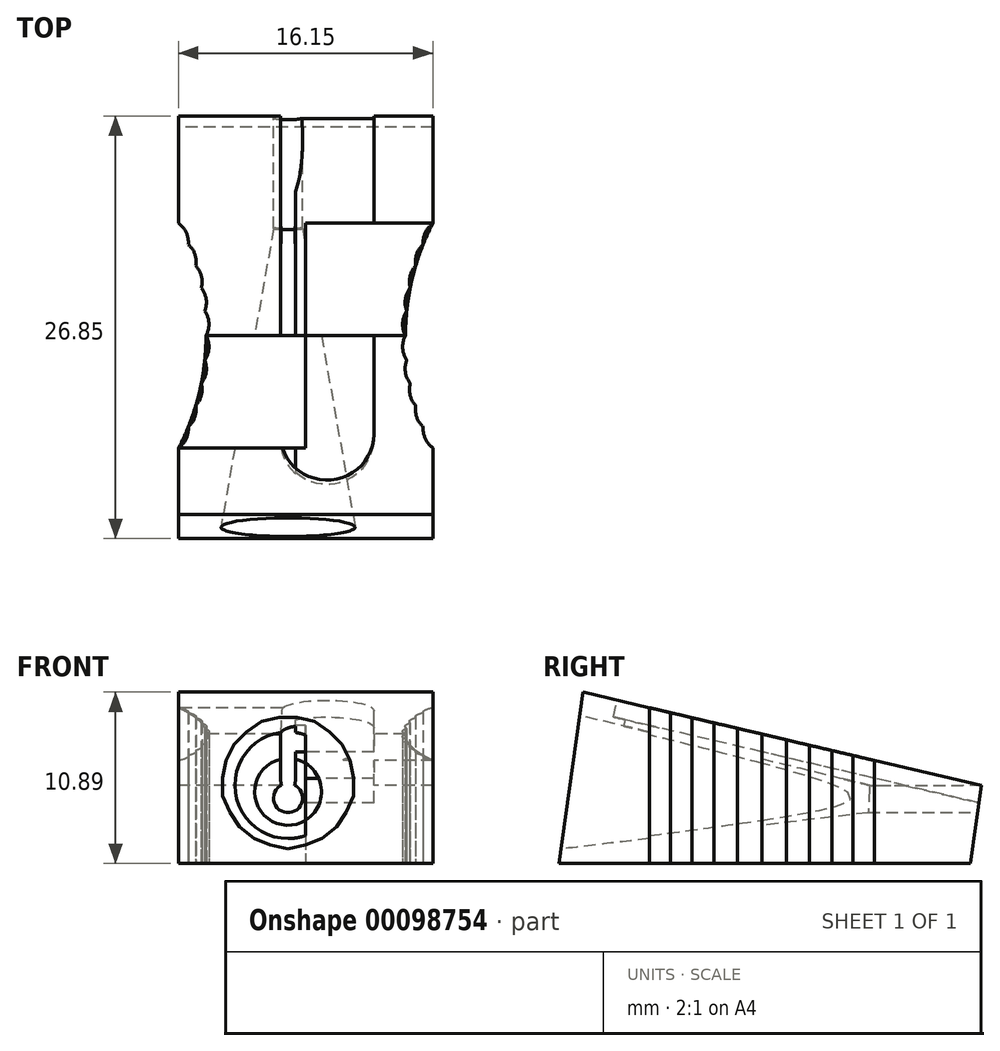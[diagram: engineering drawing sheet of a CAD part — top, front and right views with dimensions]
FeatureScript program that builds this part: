
annotation { "Feature Type Name" : "Feature", "Feature Type Description" : "" }
export const myFeature = defineFeature(function(context is Context, id is Id, definition is map)
    precondition{}
    {
        {
            var Q0;
            Q0=qCreatedBy(makeId("Right.planeOp"),FACE);
            var sketch = newSketch(context, id + "F0", { "sketchPlane" : qUnion([Q0])});
            skLineSegment(sketch, "E0.bottom", {"start": v(0, 0) * mm, "end": v(26.15, 0) * mm});
            skLineSegment(sketch, "E0.top", {"start": v(1.53, 10.9) * mm, "end": v(27.68, 10.9) * mm});
            skLineSegment(sketch, "E0.left", {"start": v(0, 0) * mm, "end": v(1.53, 10.9) * mm});
            skLineSegment(sketch, "E0.right", {"start": v(26.15, 0) * mm, "end": v(27.68, 10.9) * mm});
            skLineSegment(sketch, "E1", {"start": v(26.15, 0) * mm, "end": v(26.85, 4.95) * mm});
            skLineSegment(sketch, "E2", {"start": v(1.53, 10.9) * mm, "end": v(26.85, 4.95) * mm});
            skSolve(sketch);
        }
        {
            var Q0;
            Q0 = qSketchRegion(id + "F0", true);
            extrude(context, id + "F1", {"entities" : qUnion([Q0]), "depth" : 16.15 * mm});
        }
        {
            var Q0;
            Q0=makeQuery(id+"F0.imprint","IMPRINT",FACE,{"disambiguationData":[TD([[makeQuery(id+"F0.imprint","IMPRINT",EDGE,{"derivedFrom":sQuery(id+"F0.wireOp",EDGE,"E0.top")}),-1.0]])]});
            extrude(context, id + "F2", {"entities" : qUnion([Q0]), "operationType" : NewBodyOperationType.REMOVE, "depth" : 16.15 * mm});
        }
        {
            var Q0;
            Q0=qCreatedBy(makeId("Right.planeOp"),FACE);
            cPlane(context, id + "F3", {"entities" : qUnion([Q0]), "cplaneType" : CPlaneType.OFFSET, "offset" : 6.95 * mm, "width" : 150 * mm, "height" : 150 * mm});
        }
        {
            var Q0;
            Q0=qCreatedBy(id+"F3.planeOp",FACE);
            var sketch = newSketch(context, id + "F4", { "sketchPlane" : qUnion([Q0])});
            skLineSegment(sketch, "E3", {"start": v(0, 9.71) * mm, "end": v(19.75, 5.08) * mm});
            skLineSegment(sketch, "E4", {"start": v(19.75, 5.08) * mm, "end": v(19.75, 4.15) * mm});
            skLineSegment(sketch, "E5", {"start": v(19.75, 4.15) * mm, "end": v(0.73, 5.23) * mm});
            skLineSegment(sketch, "E6", {"start": v(0, 9.71) * mm, "end": v(0.73, 5.23) * mm});
            skLineSegment(sketch, "E7", {"start": v(19.75, 4.15) * mm, "end": v(19.75, 5.08) * mm});
            skSolve(sketch);
        }
        {
            var Q0;
            Q0=makeQuery(id+"F4.imprint","IMPRINT",FACE,{"disambiguationData":[TD([[makeQuery(id+"F4.imprint","IMPRINT",EDGE,{"derivedFrom":sQuery(id+"F4.wireOp",EDGE,"E3")}),-1.0]])]});
            var Q1;
            Q1=sQuery(id+"F4.wireOp",EDGE,"E5");
            revolve(context, id + "F5", {"operationType" : NewBodyOperationType.REMOVE, "entities" : qUnion([Q0]), "axis" : qUnion([Q1]), "revolveType" : RevolveType.FULL, "oppositeDirection" : true});
        }
        {
            var Q0;
            Q0=qCreatedBy(id+"F3.planeOp",FACE);
            var sketch = newSketch(context, id + "F6", { "sketchPlane" : qUnion([Q0])});
            skLineSegment(sketch, "E8", {"start": v(19.63, 4.17) * mm, "end": v(19.63, 5.08) * mm});
            skLineSegment(sketch, "E9", {"start": v(19.63, 5.08) * mm, "end": v(27.4, 5.1) * mm});
            skLineSegment(sketch, "E10", {"start": v(27.4, 5.1) * mm, "end": v(27.4, 4.17) * mm});
            skLineSegment(sketch, "E11", {"start": v(27.4, 4.17) * mm, "end": v(19.63, 4.17) * mm});
            skSolve(sketch);
        }
        {
            var Q0;
            Q0=makeQuery(id+"F6.imprint","IMPRINT",FACE,{"disambiguationData":[TD([[makeQuery(id+"F6.imprint","IMPRINT",EDGE,{"derivedFrom":sQuery(id+"F6.wireOp",EDGE,"E8")}),-1.0]])]});
            var Q1;
            Q1=sQuery(id+"F6.wireOp",EDGE,"E11");
            revolve(context, id + "F7", {"operationType" : NewBodyOperationType.REMOVE, "entities" : qUnion([Q0]), "axis" : qUnion([Q1]), "revolveType" : RevolveType.FULL, "oppositeDirection" : true});
        }
        {
            var Q0;
            Q0=makeQuery(id+"F2.boolean.opBoolean","COPY",FACE,{"derivedFrom":makeQuery(id+"F2.opExtrude","SWEPT_FACE",FACE,{"disambiguationData":[OSD([sQuery(id+"F0.wireOp",EDGE,"E2")])]})});
            var sketch = newSketch(context, id + "F8", { "sketchPlane" : qUnion([Q0])});
            skLineSegment(sketch, "E12", {"start": v(6.46, 25) * mm, "end": v(6.46, 4.22) * mm});
            skLineSegment(sketch, "E13", {"start": v(12.4, 25) * mm, "end": v(12.4, 4.22) * mm});
            skArc(sketch, "E14", {"start": v(6.46, 4.22) * mm, "mid": v(9.43, 1.25) * mm, "end": v(12.4, 4.22) * mm});
            skSolve(sketch);
        }
        {
            var Q0;
            Q0=makeQuery(id+"F8.imprint","IMPRINT",FACE,{"disambiguationData":[TD([[makeQuery(id+"F8.imprint","IMPRINT",EDGE,{"derivedFrom":sQuery(id+"F8.wireOp",EDGE,"E12")}),1.0]])]});
            extrude(context, id + "F9", {"entities" : qUnion([Q0]), "operationType" : NewBodyOperationType.REMOVE, "oppositeDirection" : true, "depth" : 1.1 * mm});
        }
        {
            var Q0;
            Q0=makeQuery(id+"F8.imprint","IMPRINT",FACE,{"disambiguationData":[TD([[makeQuery(id+"F8.imprint","IMPRINT",EDGE,{"derivedFrom":sQuery(id+"F8.wireOp",EDGE,"E12")}),1.0]])]});
            var sketch = newSketch(context, id + "F10", { "sketchPlane" : qUnion([Q0])});
            skLineSegment(sketch, "E15", {"start": v(7.44, 25) * mm, "end": v(7.44, 2.02) * mm});
            skSolve(sketch);
        }
        {
            var Q0;
            {var subQ0=sQuery(id+"F10.wireOp",EDGE,"E15");Q0=makeQuery(id+"F10.imprint","IMPRINT",FACE,{"disambiguationData":[TD([[makeQuery(id+"F10.imprint","IMPRINT",EDGE,{"derivedFrom":subQ0}),-1.0]])]});}
            extrude(context, id + "F11", {"entities" : qUnion([Q0]), "operationType" : NewBodyOperationType.REMOVE, "oppositeDirection" : true, "depth" : 1.6 * mm});
        }
        {
            var Q0;
            Q0=makeQuery(id+"F1.opExtrude","SWEPT_FACE",FACE,{"disambiguationData":[OSD([sQuery(id+"F0.wireOp",EDGE,"E0.bottom")])]});
            var sketch = newSketch(context, id + "F12", { "sketchPlane" : qUnion([Q0])});
            skArc(sketch, "E16", {"start": v(0, -20.03) * mm, "mid": v(1.74, -12.9) * mm, "end": v(0, -5.76) * mm});
            skArc(sketch, "E17", {"start": v(16.15, -5.76) * mm, "mid": v(14.41, -12.9) * mm, "end": v(16.15, -20.03) * mm});
            skSolve(sketch);
        }
        {
            var Q0;
            {var subQ0=sQuery(id+"F12.wireOp",EDGE,"E16");Q0=makeQuery(id+"F12.imprint","IMPRINT",FACE,{"disambiguationData":[TD([[makeQuery(id+"F12.imprint","IMPRINT",EDGE,{"derivedFrom":subQ0}),1.0]])]});}
            var Q1;
            {var subQ0=sQuery(id+"F12.wireOp",EDGE,"E17");Q1=makeQuery(id+"F12.imprint","IMPRINT",FACE,{"disambiguationData":[TD([[makeQuery(id+"F12.imprint","IMPRINT",EDGE,{"derivedFrom":subQ0}),1.0]])]});}
            extrude(context, id + "F13", {"entities" : qUnion([Q0, Q1]), "operationType" : NewBodyOperationType.REMOVE, "oppositeDirection" : true, "depth" : 10 * mm});
        }
        {
            var Q0;
            Q0=makeQuery(id+"F9.boolean.opBoolean","COPY",FACE,{"derivedFrom":makeQuery(id+"F9.opExtrude","CAP_FACE",FACE,{"disambiguationData":[OSD([sQuery(id+"F0.wireOp",EDGE,"E0.right"),sQuery(id+"F0.wireOp",EDGE,"E1"),sQuery(id+"F0.wireOp",EDGE,"E2"),sQuery(id+"F6.wireOp",EDGE,"E9"),sQuery(id+"F8.wireOp",EDGE,"E12"),sQuery(id+"F8.wireOp",EDGE,"E13"),sQuery(id+"F8.wireOp",EDGE,"E14")])],"isStart":false})});
            var sketch = newSketch(context, id + "F14", { "sketchPlane" : qUnion([Q0])});
            skLineSegment(sketch, "E18", {"start": v(12.4, 25) * mm, "end": v(12.4, 4.22) * mm});
            skLineSegment(sketch, "E19", {"start": v(7.44, 25) * mm, "end": v(7.83, 25) * mm});
            skLineSegment(sketch, "E20", {"start": v(7.83, 25) * mm, "end": v(7.83, 1.72) * mm});
            skSolve(sketch);
        }
        {
            var Q0;
            Q0=makeQuery(id+"F9.boolean.opBoolean","COPY",FACE,{"derivedFrom":makeQuery(id+"F9.opExtrude","SWEPT_FACE",FACE,{"disambiguationData":[OSD([sQuery(id+"F0.wireOp",EDGE,"E0.right"),sQuery(id+"F0.wireOp",EDGE,"E1"),sQuery(id+"F0.wireOp",EDGE,"E2")])]})});
            extrude(context, id + "F15", {"entities" : qUnion([Q0]), "operationType" : NewBodyOperationType.REMOVE, "oppositeDirection" : true, "depth" : 25 * mm});
        }
        {
            var Q0;
            {var subQ0=sQuery(id+"F14.wireOp",EDGE,"E18");Q0=makeQuery(id+"F14.imprint","IMPRINT",FACE,{"disambiguationData":[TD([[makeQuery(id+"F14.imprint","IMPRINT",EDGE,{"derivedFrom":subQ0}),-1.0]])]});}
            var sketch = newSketch(context, id + "F16", { "sketchPlane" : qUnion([Q0])});
            skCircle(sketch, "E21", {"center": v(10.67, 12.1) * mm, "radius": 1.08 * mm});
            skSolve(sketch);
        }
        {
            var Q0;
            Q0=makeQuery(id+"F16.imprint","IMPRINT",FACE,{"disambiguationData":[TD([[makeQuery(id+"F16.imprint","IMPRINT",EDGE,{"derivedFrom":sQuery(id+"F16.wireOp",EDGE,"E21")}),1.0]])]});
            extrude(context, id + "F17", {"entities" : qUnion([Q0]), "operationType" : NewBodyOperationType.REMOVE, "oppositeDirection" : true, "depth" : .5 * mm});
        }
        {
            var Q0;
            Q0=makeQuery(id+"F1.opExtrude","SWEPT_FACE",FACE,{"disambiguationData":[OSD([sQuery(id+"F0.wireOp",EDGE,"E0.bottom")])]});
            var sketch = newSketch(context, id + "F18", { "sketchPlane" : qUnion([Q0])});
            skLineSegment(sketch, "E22", {"start": v(1.74, -12.9) * mm, "end": v(14.41, -12.9) * mm});
            skLineSegment(sketch, "E23", {"start": v(0, -5.76) * mm, "end": v(16.15, -5.76) * mm});
            skLineSegment(sketch, "E24", {"start": v(0, -20.03) * mm, "end": v(16.15, -20.03) * mm});
            skLineSegment(sketch, "E25", {"start": v(8.07, -5.76) * mm, "end": v(8.07, -20.03) * mm});
            skLineSegment(sketch, "E26.MirrorCS", {"start": v(14.41, -12.9) * mm, "end": v(1.74, -12.9) * mm});
            skPoint(sketch, "E27", {"position": v(0.61, -18.7) * mm});
            skPoint(sketch, "E28", {"position": v(1.1, -17.33) * mm});
            skPoint(sketch, "E29", {"position": v(1.44, -15.93) * mm});
            skPoint(sketch, "E30", {"position": v(1.66, -14.46) * mm});
            skArc(sketch, "E31", {"start": v(0, -20.03) * mm, "mid": v(0.49, -19.44) * mm, "end": v(0.61, -18.7) * mm});
            skArc(sketch, "E32", {"start": v(0.61, -18.7) * mm, "mid": v(1.03, -18.07) * mm, "end": v(1.1, -17.33) * mm});
            skArc(sketch, "E33", {"start": v(1.1, -17.33) * mm, "mid": v(1.45, -16.68) * mm, "end": v(1.44, -15.93) * mm});
            skArc(sketch, "E34", {"start": v(1.44, -15.93) * mm, "mid": v(1.75, -15.22) * mm, "end": v(1.66, -14.46) * mm});
            skArc(sketch, "E35", {"start": v(1.66, -14.46) * mm, "mid": v(1.92, -13.69) * mm, "end": v(1.74, -12.9) * mm});
            skArc(sketch, "E36", {"start": v(-0.86, -18.83) * mm, "mid": v(0.02, -16.28) * mm, "end": v(0.45, -13.61) * mm, "construction": true});
            skArc(sketch, "E37.MirrorCS", {"start": v(1.66, -11.34) * mm, "mid": v(1.92, -12.1) * mm, "end": v(1.74, -12.9) * mm});
            skArc(sketch, "E38.MirrorCS", {"start": v(1.44, -9.87) * mm, "mid": v(1.75, -10.57) * mm, "end": v(1.66, -11.34) * mm});
            skArc(sketch, "E39.MirrorCS", {"start": v(1.1, -8.46) * mm, "mid": v(1.45, -9.12) * mm, "end": v(1.44, -9.87) * mm});
            skArc(sketch, "E40.MirrorCS", {"start": v(0.61, -7.1) * mm, "mid": v(1.03, -7.72) * mm, "end": v(1.1, -8.46) * mm});
            skArc(sketch, "E41.MirrorCS", {"start": v(0, -5.76) * mm, "mid": v(0.49, -6.35) * mm, "end": v(0.61, -7.1) * mm});
            skArc(sketch, "E42.MirrorCS", {"start": v(16.15, -5.76) * mm, "mid": v(15.66, -6.35) * mm, "end": v(15.54, -7.1) * mm});
            skArc(sketch, "E43.MirrorCS", {"start": v(15.54, -7.1) * mm, "mid": v(15.12, -7.72) * mm, "end": v(15.06, -8.46) * mm});
            skArc(sketch, "E44.MirrorCS", {"start": v(15.06, -8.46) * mm, "mid": v(14.7, -9.12) * mm, "end": v(14.71, -9.87) * mm});
            skArc(sketch, "E45.MirrorCS", {"start": v(14.71, -9.87) * mm, "mid": v(14.4, -10.57) * mm, "end": v(14.5, -11.34) * mm});
            skArc(sketch, "E46.MirrorCS", {"start": v(14.5, -11.34) * mm, "mid": v(14.23, -12.1) * mm, "end": v(14.41, -12.9) * mm});
            skArc(sketch, "E47.MirrorCS", {"start": v(14.5, -14.46) * mm, "mid": v(14.23, -13.69) * mm, "end": v(14.41, -12.9) * mm});
            skArc(sketch, "E48.MirrorCS", {"start": v(14.71, -15.93) * mm, "mid": v(14.4, -15.22) * mm, "end": v(14.5, -14.46) * mm});
            skArc(sketch, "E49.MirrorCS", {"start": v(15.06, -17.33) * mm, "mid": v(14.7, -16.68) * mm, "end": v(14.71, -15.93) * mm});
            skArc(sketch, "E50.MirrorCS", {"start": v(15.54, -18.7) * mm, "mid": v(15.12, -18.07) * mm, "end": v(15.06, -17.33) * mm});
            skArc(sketch, "E51.MirrorCS", {"start": v(16.15, -20.03) * mm, "mid": v(15.66, -19.44) * mm, "end": v(15.54, -18.7) * mm});
            skSolve(sketch);
        }
        {
            var Q0;
            {var subQ0=sQuery(id+"F18.wireOp",EDGE,"E35");Q0=makeQuery(id+"F18.imprint","IMPRINT",FACE,{"disambiguationData":[TD([[makeQuery(id+"F18.imprint","IMPRINT",EDGE,{"derivedFrom":subQ0}),1.0]])]});}
            var Q1;
            {var subQ0=sQuery(id+"F18.wireOp",EDGE,"E34");Q1=makeQuery(id+"F18.imprint","IMPRINT",FACE,{"disambiguationData":[TD([[makeQuery(id+"F18.imprint","IMPRINT",EDGE,{"derivedFrom":subQ0}),1.0]])]});}
            var Q2;
            {var subQ0=sQuery(id+"F18.wireOp",EDGE,"E33");Q2=makeQuery(id+"F18.imprint","IMPRINT",FACE,{"disambiguationData":[TD([[makeQuery(id+"F18.imprint","IMPRINT",EDGE,{"derivedFrom":subQ0}),1.0]])]});}
            var Q3;
            {var subQ0=sQuery(id+"F18.wireOp",EDGE,"E32");Q3=makeQuery(id+"F18.imprint","IMPRINT",FACE,{"disambiguationData":[TD([[makeQuery(id+"F18.imprint","IMPRINT",EDGE,{"derivedFrom":subQ0}),1.0]])]});}
            var Q4;
            {var subQ0=sQuery(id+"F18.wireOp",EDGE,"E31");Q4=makeQuery(id+"F18.imprint","IMPRINT",FACE,{"disambiguationData":[TD([[makeQuery(id+"F18.imprint","IMPRINT",EDGE,{"derivedFrom":subQ0}),1.0]])]});}
            var Q5;
            {var subQ0=sQuery(id+"F18.wireOp",EDGE,"E37.MirrorCS");Q5=makeQuery(id+"F18.imprint","IMPRINT",FACE,{"disambiguationData":[TD([[makeQuery(id+"F18.imprint","IMPRINT",EDGE,{"derivedFrom":subQ0}),-1.0]])]});}
            var Q6;
            {var subQ0=sQuery(id+"F18.wireOp",EDGE,"E38.MirrorCS");Q6=makeQuery(id+"F18.imprint","IMPRINT",FACE,{"disambiguationData":[TD([[makeQuery(id+"F18.imprint","IMPRINT",EDGE,{"derivedFrom":subQ0}),-1.0]])]});}
            var Q7;
            {var subQ0=sQuery(id+"F18.wireOp",EDGE,"E39.MirrorCS");Q7=makeQuery(id+"F18.imprint","IMPRINT",FACE,{"disambiguationData":[TD([[makeQuery(id+"F18.imprint","IMPRINT",EDGE,{"derivedFrom":subQ0}),-1.0]])]});}
            var Q8;
            {var subQ0=sQuery(id+"F18.wireOp",EDGE,"E40.MirrorCS");Q8=makeQuery(id+"F18.imprint","IMPRINT",FACE,{"disambiguationData":[TD([[makeQuery(id+"F18.imprint","IMPRINT",EDGE,{"derivedFrom":subQ0}),-1.0]])]});}
            var Q9;
            {var subQ0=sQuery(id+"F18.wireOp",EDGE,"E41.MirrorCS");Q9=makeQuery(id+"F18.imprint","IMPRINT",FACE,{"disambiguationData":[TD([[makeQuery(id+"F18.imprint","IMPRINT",EDGE,{"derivedFrom":subQ0}),-1.0]])]});}
            var Q10;
            {var subQ0=sQuery(id+"F18.wireOp",EDGE,"E42.MirrorCS");Q10=makeQuery(id+"F18.imprint","IMPRINT",FACE,{"disambiguationData":[TD([[makeQuery(id+"F18.imprint","IMPRINT",EDGE,{"derivedFrom":subQ0}),1.0]])]});}
            var Q11;
            {var subQ0=sQuery(id+"F18.wireOp",EDGE,"E43.MirrorCS");Q11=makeQuery(id+"F18.imprint","IMPRINT",FACE,{"disambiguationData":[TD([[makeQuery(id+"F18.imprint","IMPRINT",EDGE,{"derivedFrom":subQ0}),1.0]])]});}
            var Q12;
            {var subQ0=sQuery(id+"F18.wireOp",EDGE,"E44.MirrorCS");Q12=makeQuery(id+"F18.imprint","IMPRINT",FACE,{"disambiguationData":[TD([[makeQuery(id+"F18.imprint","IMPRINT",EDGE,{"derivedFrom":subQ0}),1.0]])]});}
            var Q13;
            {var subQ0=sQuery(id+"F18.wireOp",EDGE,"E45.MirrorCS");Q13=makeQuery(id+"F18.imprint","IMPRINT",FACE,{"disambiguationData":[TD([[makeQuery(id+"F18.imprint","IMPRINT",EDGE,{"derivedFrom":subQ0}),1.0]])]});}
            var Q14;
            {var subQ0=sQuery(id+"F18.wireOp",EDGE,"E46.MirrorCS");Q14=makeQuery(id+"F18.imprint","IMPRINT",FACE,{"disambiguationData":[TD([[makeQuery(id+"F18.imprint","IMPRINT",EDGE,{"derivedFrom":subQ0}),1.0]])]});}
            var Q15;
            {var subQ0=sQuery(id+"F18.wireOp",EDGE,"E47.MirrorCS");Q15=makeQuery(id+"F18.imprint","IMPRINT",FACE,{"disambiguationData":[TD([[makeQuery(id+"F18.imprint","IMPRINT",EDGE,{"derivedFrom":subQ0}),-1.0]])]});}
            var Q16;
            {var subQ0=sQuery(id+"F18.wireOp",EDGE,"E48.MirrorCS");Q16=makeQuery(id+"F18.imprint","IMPRINT",FACE,{"disambiguationData":[TD([[makeQuery(id+"F18.imprint","IMPRINT",EDGE,{"derivedFrom":subQ0}),-1.0]])]});}
            var Q17;
            {var subQ0=sQuery(id+"F18.wireOp",EDGE,"E49.MirrorCS");Q17=makeQuery(id+"F18.imprint","IMPRINT",FACE,{"disambiguationData":[TD([[makeQuery(id+"F18.imprint","IMPRINT",EDGE,{"derivedFrom":subQ0}),-1.0]])]});}
            var Q18;
            {var subQ0=sQuery(id+"F18.wireOp",EDGE,"E50.MirrorCS");Q18=makeQuery(id+"F18.imprint","IMPRINT",FACE,{"disambiguationData":[TD([[makeQuery(id+"F18.imprint","IMPRINT",EDGE,{"derivedFrom":subQ0}),-1.0]])]});}
            var Q19;
            {var subQ0=sQuery(id+"F18.wireOp",EDGE,"E51.MirrorCS");Q19=makeQuery(id+"F18.imprint","IMPRINT",FACE,{"disambiguationData":[TD([[makeQuery(id+"F18.imprint","IMPRINT",EDGE,{"derivedFrom":subQ0}),-1.0]])]});}
            extrude(context, id + "F19", {"entities" : qUnion([Q0, Q1, Q2, Q3, Q4, Q5, Q6, Q7, Q8, Q9, Q10, Q11, Q12, Q13, Q14, Q15, Q16, Q17, Q18, Q19]), "operationType" : NewBodyOperationType.REMOVE, "oppositeDirection" : true, "depth" : 10 * mm});
        }
    });
